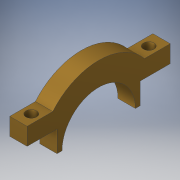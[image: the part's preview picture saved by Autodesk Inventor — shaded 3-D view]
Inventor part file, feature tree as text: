
AUTODESK INVENTOR PART (.ipt)
format: ipt  version: 2019 (Build 230136000, 136)  size: 129,536 bytes
history: native  units: mm
features: extrude x2, sketch x2
ambient origin geometry x8: Origin, YZ Plane, XZ Plane, XY Plane, X Axis, Y Axis, Z Axis, Center Point
bodies: Solid1 (feature_tree)
feature tree (4):
  extrude  "Extrusion1"  Depth=185.0mm
  extrude  "Extrusion2"  Depth=1122.5mm
  sketch  "Sketch1"  dims[d3=185.0mm d4=185.0mm]
  sketch  "Sketch2"  dims[d5=800.0mm d6=1122.5mm d7=800.0mm d8=1122.5mm d9=650.0mm d10=650.0mm d11=650.0mm d12=0.0mm d19=7000.0mm d20=0.0mm]
